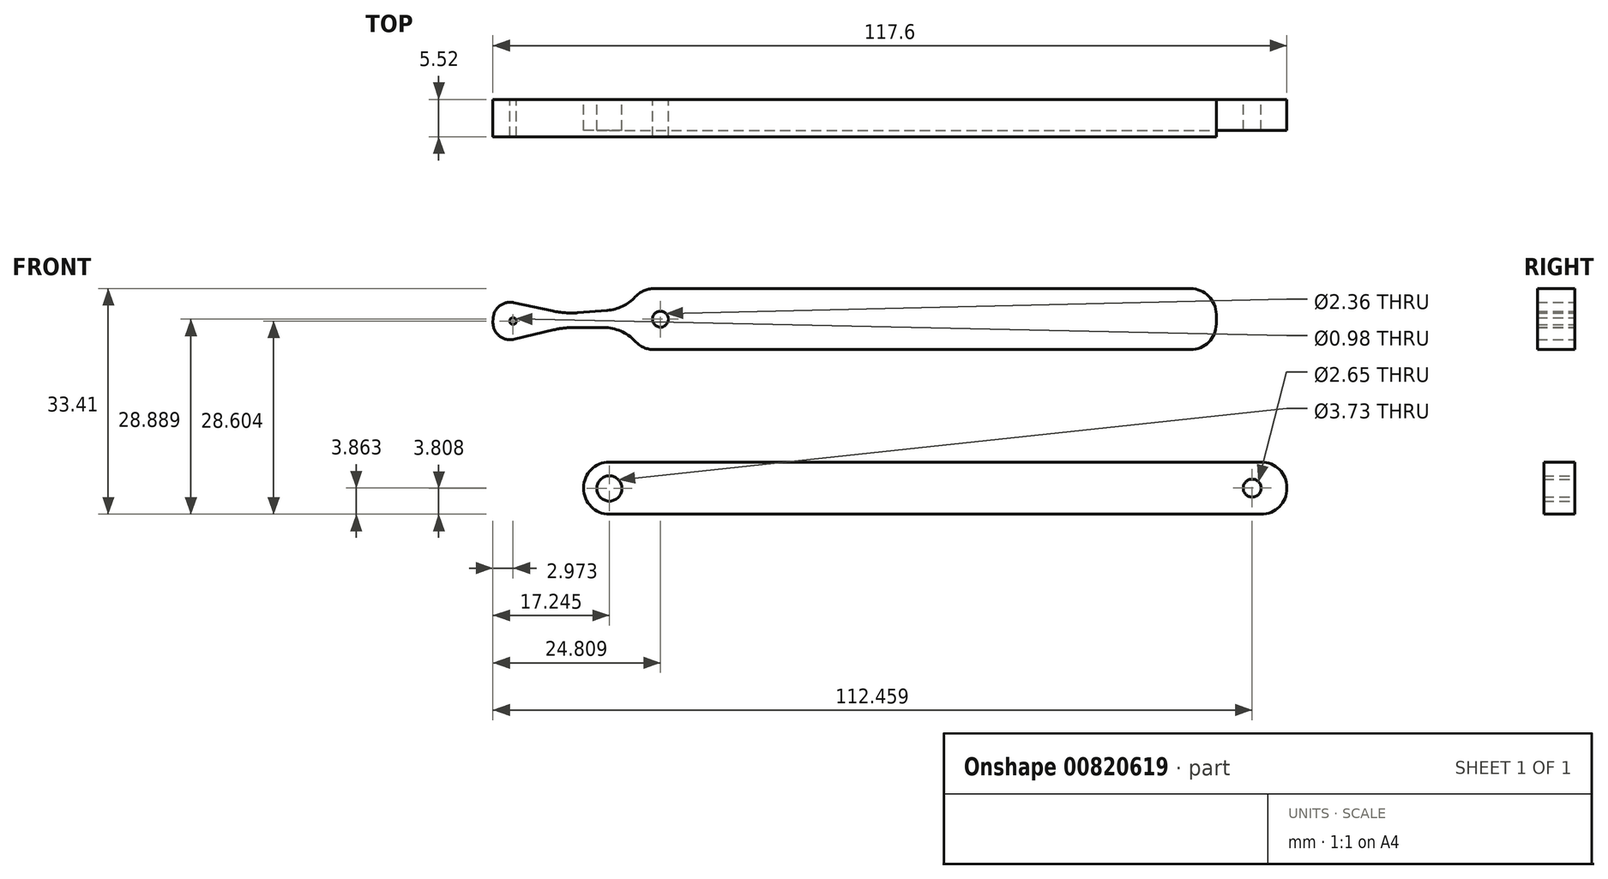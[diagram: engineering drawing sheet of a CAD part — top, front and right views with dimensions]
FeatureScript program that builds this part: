
annotation { "Feature Type Name" : "Feature", "Feature Type Description" : "" }
export const myFeature = defineFeature(function(context is Context, id is Id, definition is map)
    precondition{}
    {
        {
            var Q0;
            Q0=qCreatedBy(makeId("Front.planeOp"),FACE);
            var sketch = newSketch(context, id + "F0", { "sketchPlane" : qUnion([Q0])});
            skLineSegment(sketch, "E0.bottom", {"start": v(-47.66, 33.63) * mm, "end": v(48.88, 33.63) * mm});
            skLineSegment(sketch, "E0.top", {"start": v(-47.66, 25.9) * mm, "end": v(48.88, 25.9) * mm});
            skLineSegment(sketch, "E0.left", {"start": v(-51.47, 29.82) * mm, "end": v(-51.47, 29.7) * mm});
            skLineSegment(sketch, "E0.right", {"start": v(52.69, 29.82) * mm, "end": v(52.69, 29.7) * mm});
            skPoint(sketch, "E1.visualSharp", {"position": v(52.69, 25.9) * mm});
            skArc(sketch, "E1.filletArc", {"start": v(48.88, 25.9) * mm, "mid": v(51.57, 27.01) * mm, "end": v(52.69, 29.7) * mm});
            skPoint(sketch, "E2.visualSharp", {"position": v(52.69, 33.63) * mm});
            skArc(sketch, "E2.filletArc", {"start": v(52.69, 29.82) * mm, "mid": v(51.57, 32.51) * mm, "end": v(48.88, 33.63) * mm});
            skCircle(sketch, "E3", {"center": v(47.55, 29.76) * mm, "radius": 1.33 * mm});
            skPoint(sketch, "E3.third.point", {"position": v(48.86, 29.95) * mm});
            skPoint(sketch, "E4.visualSharp", {"position": v(-51.47, 25.9) * mm});
            skArc(sketch, "E4.filletArc", {"start": v(-51.47, 29.7) * mm, "mid": v(-50.36, 27.01) * mm, "end": v(-47.66, 25.9) * mm});
            skPoint(sketch, "E5.visualSharp", {"position": v(-51.47, 33.63) * mm});
            skArc(sketch, "E5.filletArc", {"start": v(-47.66, 33.63) * mm, "mid": v(-50.36, 32.51) * mm, "end": v(-51.47, 29.82) * mm});
            skCircle(sketch, "E6", {"center": v(-47.66, 29.7) * mm, "radius": 1.87 * mm});
            skSolve(sketch);
        }
        {
            var Q0;
            Q0=makeQuery(id+"F0.imprint","IMPRINT",FACE,{"disambiguationData":[TD([[makeQuery(id+"F0.imprint","IMPRINT",EDGE,{"derivedFrom":sQuery(id+"F0.wireOp",EDGE,"E0.bottom")}),-1.0]])]});
            extrude(context, id + "F1", {"entities" : qUnion([Q0]), "depth" : 4.56 * mm, "offsetDistance" : 25.4 * mm});
        }
        {
            var Q0;
            Q0=qCreatedBy(makeId("Front.planeOp"),FACE);
            var sketch = newSketch(context, id + "F2", { "sketchPlane" : qUnion([Q0])});
            skLineSegment(sketch, "E7.bottom", {"start": v(-41.04, 59.3) * mm, "end": v(38.42, 59.3) * mm});
            skLineSegment(sketch, "E7.top", {"start": v(-41.04, 50.27) * mm, "end": v(38.42, 50.27) * mm});
            skLineSegment(sketch, "E7.left", {"start": v(-44.85, 55.5) * mm, "end": v(-44.85, 54.08) * mm});
            skLineSegment(sketch, "E7.right", {"start": v(42.23, 55.5) * mm, "end": v(42.23, 54.08) * mm});
            skPoint(sketch, "E8.visualSharp", {"position": v(-44.85, 50.27) * mm});
            skArc(sketch, "E8.filletArc", {"start": v(-43.85, 51.5) * mm, "mid": v(-42.58, 50.6) * mm, "end": v(-41.04, 50.27) * mm});
            skPoint(sketch, "E9.visualSharp", {"position": v(-44.85, 59.3) * mm});
            skArc(sketch, "E9.filletArc", {"start": v(-41.04, 59.3) * mm, "mid": v(-42.57, 59) * mm, "end": v(-43.83, 58.1) * mm});
            skLineSegment(sketch, "E10", {"start": v(-48.52, 53.55) * mm, "end": v(-52.97, 53.55) * mm});
            skLineSegment(sketch, "E11", {"start": v(-47.97, 56.1) * mm, "end": v(-52.34, 55.74) * mm});
            skLineSegment(sketch, "E12", {"start": v(-54.46, 53.55) * mm, "end": v(-54.22, 55.6) * mm});
            skArc(sketch, "E13.filletArc", {"start": v(-43.85, 51.5) * mm, "mid": v(-45.97, 53.02) * mm, "end": v(-48.52, 53.55) * mm});
            skArc(sketch, "E14.filletArc", {"start": v(-47.97, 56.1) * mm, "mid": v(-45.71, 56.7) * mm, "end": v(-43.83, 58.1) * mm});
            skLineSegment(sketch, "E15", {"start": v(-55.9, 53.2) * mm, "end": v(-61.78, 51.8) * mm});
            skLineSegment(sketch, "E16", {"start": v(-56.06, 56) * mm, "end": v(-61.81, 57.24) * mm});
            skLineSegment(sketch, "E17", {"start": v(-64.9, 54.37) * mm, "end": v(-64.89, 54.85) * mm});
            skPoint(sketch, "E18.visualSharp", {"position": v(-54.46, 53.55) * mm});
            skArc(sketch, "E18.filletArc", {"start": v(-52.97, 53.55) * mm, "mid": v(-54.45, 53.46) * mm, "end": v(-55.9, 53.2) * mm});
            skPoint(sketch, "E19.visualSharp", {"position": v(-54.22, 55.6) * mm});
            skArc(sketch, "E19.filletArc", {"start": v(-56.06, 56) * mm, "mid": v(-54.2, 55.73) * mm, "end": v(-52.34, 55.74) * mm});
            skPoint(sketch, "E20.visualSharp", {"position": v(-65.03, 51.03) * mm});
            skArc(sketch, "E20.filletArc", {"start": v(-64.9, 54.37) * mm, "mid": v(-63.98, 52.31) * mm, "end": v(-61.78, 51.8) * mm});
            skPoint(sketch, "E21.visualSharp", {"position": v(-64.78, 57.89) * mm});
            skArc(sketch, "E21.filletArc", {"start": v(-61.81, 57.24) * mm, "mid": v(-63.9, 56.77) * mm, "end": v(-64.89, 54.85) * mm});
            skCircle(sketch, "E22", {"center": v(-40.1, 54.79) * mm, "radius": 1.18 * mm});
            skPoint(sketch, "E22.third.point", {"position": v(-38.93, 54.94) * mm});
            skCircle(sketch, "E23", {"center": v(-61.94, 54.5) * mm, "radius": 0.49 * mm});
            skPoint(sketch, "E23.third.point", {"position": v(-61.45, 54.5) * mm});
            skPoint(sketch, "E24.visualSharp", {"position": v(42.23, 50.27) * mm});
            skArc(sketch, "E24.filletArc", {"start": v(38.42, 50.27) * mm, "mid": v(41.1, 51.39) * mm, "end": v(42.23, 54.08) * mm});
            skPoint(sketch, "E25.visualSharp", {"position": v(42.23, 59.3) * mm});
            skArc(sketch, "E25.filletArc", {"start": v(42.23, 55.5) * mm, "mid": v(41.1, 58.2) * mm, "end": v(38.42, 59.3) * mm});
            skSolve(sketch);
        }
        {
            var Q0;
            Q0 = qSketchRegion(id + "F2", true);
            var Q1;
            Q1=makeQuery(id+"F2.imprint","IMPRINT",FACE,{"disambiguationData":[TD([[makeQuery(id+"F2.imprint","IMPRINT",EDGE,{"derivedFrom":sQuery(id+"F2.wireOp",EDGE,"E7.bottom")}),-1.0]])]});
            extrude(context, id + "F3", {"entities" : qUnion([Q0, Q1]), "depth" : 5.52 * mm, "offsetDistance" : 25.4 * mm});
        }
    });
